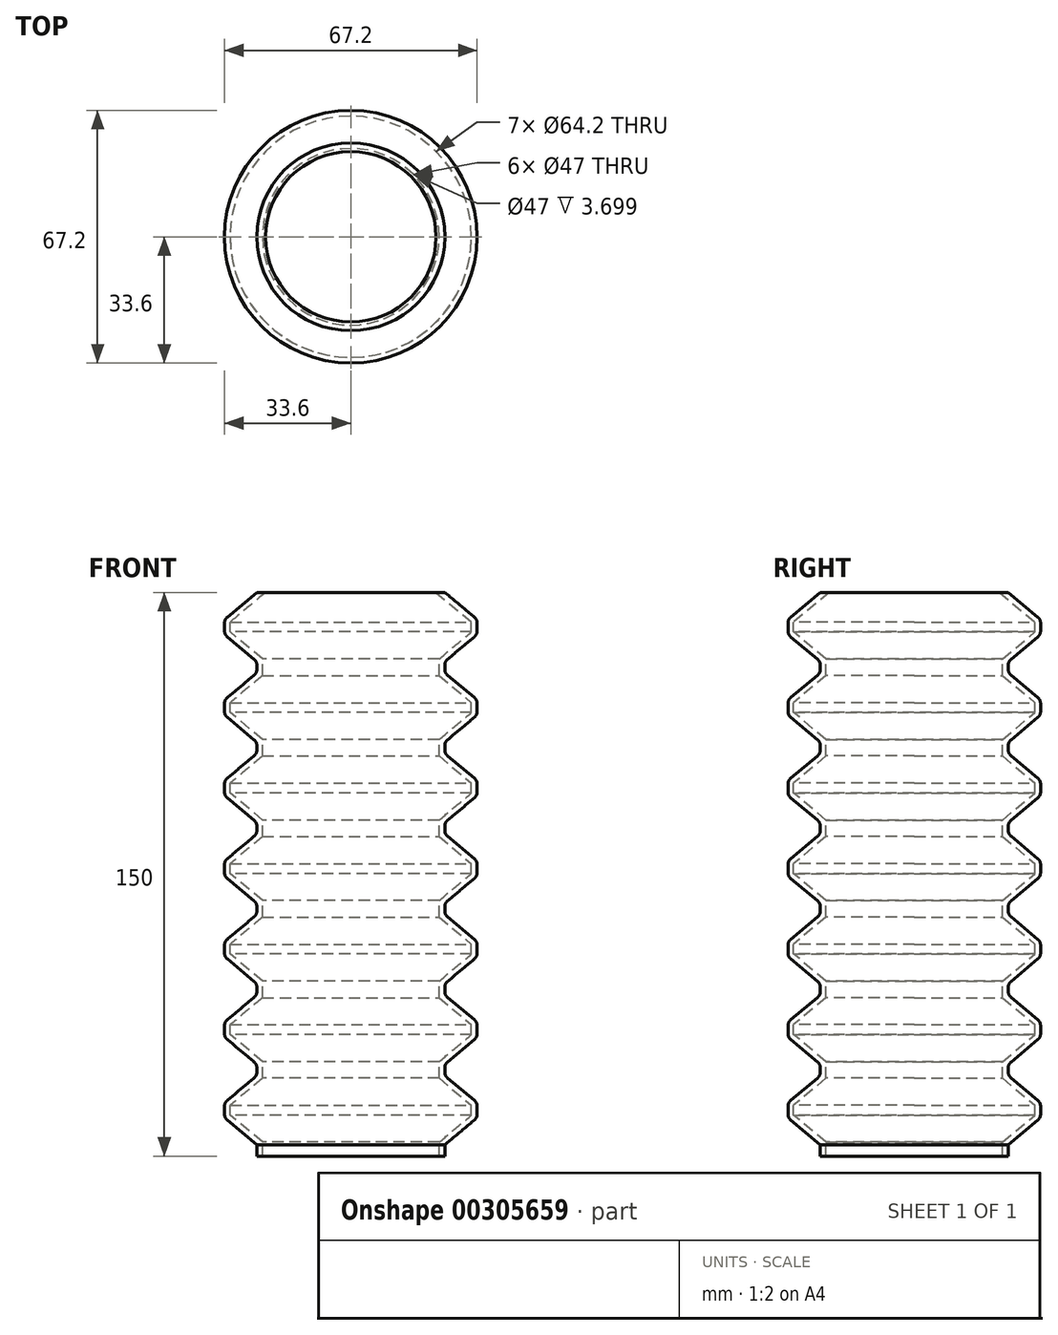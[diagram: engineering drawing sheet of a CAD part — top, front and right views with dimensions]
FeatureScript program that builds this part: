
annotation { "Feature Type Name" : "Feature", "Feature Type Description" : "" }
export const myFeature = defineFeature(function(context is Context, id is Id, definition is map)
    precondition{}
    {
        {
            var Q0;
            Q0=qCreatedBy(makeId("Front.planeOp"),FACE);
            var sketch = newSketch(context, id + "F0", { "sketchPlane" : qUnion([Q0])});
            skLineSegment(sketch, "E0", {"start": v(0, 145.92) * mm, "end": v(0, -99.97) * mm, "construction": true});
            skLineSegment(sketch, "E1", {"start": v(0, -21.95) * mm, "end": v(-25, -21.95) * mm});
            skLineSegment(sketch, "E2", {"start": v(-25, -21.95) * mm, "end": v(-25, -18.95) * mm});
            skLineSegment(sketch, "E3", {"start": v(-25, -18.95) * mm, "end": v(-33.6, -11.74) * mm});
            skLineSegment(sketch, "E4", {"start": v(-33.6, -11.74) * mm, "end": v(-33.6, -7.74) * mm});
            skLineSegment(sketch, "E5", {"start": v(-25, 2.48) * mm, "end": v(-33.6, 9.7) * mm});
            skLineSegment(sketch, "E6", {"start": v(-33.6, 9.7) * mm, "end": v(-33.6, 13.7) * mm});
            skLineSegment(sketch, "E7", {"start": v(-33.6, 13.7) * mm, "end": v(-25, 20.9) * mm});
            skLineSegment(sketch, "E8", {"start": v(-25, 20.9) * mm, "end": v(-25, 23.9) * mm});
            skLineSegment(sketch, "E9", {"start": v(-25, 23.9) * mm, "end": v(-33.6, 31.12) * mm});
            skLineSegment(sketch, "E10", {"start": v(-33.6, 31.12) * mm, "end": v(-33.6, 35.12) * mm});
            skLineSegment(sketch, "E11", {"start": v(-33.6, 35.12) * mm, "end": v(-25, 42.33) * mm});
            skLineSegment(sketch, "E12", {"start": v(-25, 42.33) * mm, "end": v(-25, 45.33) * mm});
            skLineSegment(sketch, "E13", {"start": v(-25, 45.33) * mm, "end": v(-33.6, 52.55) * mm});
            skLineSegment(sketch, "E14", {"start": v(-33.6, 52.55) * mm, "end": v(-33.6, 56.55) * mm});
            skLineSegment(sketch, "E15", {"start": v(-33.6, 56.55) * mm, "end": v(-25, 63.76) * mm});
            skLineSegment(sketch, "E16", {"start": v(-33.6, 73.98) * mm, "end": v(-33.6, 77.98) * mm});
            skLineSegment(sketch, "E17", {"start": v(-33.6, 77.98) * mm, "end": v(-25, 85.2) * mm});
            skLineSegment(sketch, "E18", {"start": v(-25, 85.2) * mm, "end": v(-25, 88.2) * mm});
            skLineSegment(sketch, "E19", {"start": v(-25, 88.2) * mm, "end": v(-33.6, 95.4) * mm});
            skLineSegment(sketch, "E20", {"start": v(-33.6, 95.4) * mm, "end": v(-33.6, 99.4) * mm});
            skLineSegment(sketch, "E21", {"start": v(-33.6, 99.4) * mm, "end": v(-25, 106.62) * mm});
            skLineSegment(sketch, "E22", {"start": v(-25, 106.62) * mm, "end": v(-25, 109.62) * mm});
            skLineSegment(sketch, "E23", {"start": v(-25, 109.62) * mm, "end": v(-33.6, 116.83) * mm});
            skLineSegment(sketch, "E24", {"start": v(-33.6, 116.83) * mm, "end": v(-33.6, 120.83) * mm});
            skLineSegment(sketch, "E25", {"start": v(-33.6, 120.83) * mm, "end": v(-25, 128.05) * mm});
            skLineSegment(sketch, "E26", {"start": v(-25, 63.76) * mm, "end": v(-25, 66.76) * mm});
            skLineSegment(sketch, "E27", {"start": v(-25, 66.76) * mm, "end": v(-33.6, 73.98) * mm});
            skLineSegment(sketch, "E28", {"start": v(-25, 2.48) * mm, "end": v(-25, -0.52) * mm});
            skLineSegment(sketch, "E29", {"start": v(-25, -0.52) * mm, "end": v(-33.6, -7.74) * mm});
            skLineSegment(sketch, "E30", {"start": v(-25, 128.05) * mm, "end": v(0, 128.05) * mm});
            skLineSegment(sketch, "E31", {"start": v(0, 128.05) * mm, "end": v(0, -21.95) * mm});
            skSolve(sketch);
        }
        {
            var Q0;
            Q0=makeQuery(id+"F0.imprint","IMPRINT",FACE,{"disambiguationData":[TD([[makeQuery(id+"F0.imprint","IMPRINT",EDGE,{"derivedFrom":sQuery(id+"F0.wireOp",EDGE,"E1")}),-1.0]])]});
            var Q1;
            Q1=sQuery(id+"F0.wireOp",EDGE,"E0");
            revolve(context, id + "F1", {"entities" : qUnion([Q0]), "axis" : qUnion([Q1]), "revolveType" : RevolveType.FULL});
        }
        {
            var Q0;
            Q0=makeQuery(id+"F1.opRevolve","SWEPT_FACE",FACE,{"disambiguationData":[OSD([sQuery(id+"F0.wireOp",EDGE,"E30")])]});
            var Q1;
            Q1=makeQuery(id+"F1.opRevolve","SWEPT_FACE",FACE,{"disambiguationData":[OSD([sQuery(id+"F0.wireOp",EDGE,"E1")])]});
            shell(context, id + "F2", {"entities" : qUnion([Q0, Q1]), "thickness" : 1.5 * mm});
        }
        {
            var Q0;
            Q0=makeQuery(id+"F1.opRevolve","SWEPT_FACE",FACE,{"disambiguationData":[OSD([sQuery(id+"F0.wireOp",EDGE,"E24")])]});
            var Q1;
            Q1=makeQuery(id+"F1.opRevolve","SWEPT_FACE",FACE,{"disambiguationData":[OSD([sQuery(id+"F0.wireOp",EDGE,"E20")])]});
            var Q2;
            Q2=makeQuery(id+"F1.opRevolve","SWEPT_FACE",FACE,{"disambiguationData":[OSD([sQuery(id+"F0.wireOp",EDGE,"E16")])]});
            var Q3;
            Q3=makeQuery(id+"F1.opRevolve","SWEPT_FACE",FACE,{"disambiguationData":[OSD([sQuery(id+"F0.wireOp",EDGE,"E14")])]});
            var Q4;
            Q4=makeQuery(id+"F1.opRevolve","SWEPT_FACE",FACE,{"disambiguationData":[OSD([sQuery(id+"F0.wireOp",EDGE,"E10")])]});
            var Q5;
            Q5=makeQuery(id+"F1.opRevolve","SWEPT_FACE",FACE,{"disambiguationData":[OSD([sQuery(id+"F0.wireOp",EDGE,"E6")])]});
            var Q6;
            Q6=makeQuery(id+"F1.opRevolve","SWEPT_FACE",FACE,{"disambiguationData":[OSD([sQuery(id+"F0.wireOp",EDGE,"E4")])]});
            fillet(context, id + "F3", {"entities" : qUnion([Q0, Q1, Q2, Q3, Q4, Q5, Q6]), "radius" : 2 * mm, "tangentPropagation" : true, "allowEdgeOverflow" : false});
        }
        {
            var Q0;
            Q0=makeQuery(id+"F1.opRevolve","SWEPT_FACE",FACE,{"disambiguationData":[OSD([sQuery(id+"F0.wireOp",EDGE,"E22")])]});
            var Q1;
            Q1=makeQuery(id+"F1.opRevolve","SWEPT_FACE",FACE,{"disambiguationData":[OSD([sQuery(id+"F0.wireOp",EDGE,"E18")])]});
            var Q2;
            Q2=makeQuery(id+"F1.opRevolve","SWEPT_FACE",FACE,{"disambiguationData":[OSD([sQuery(id+"F0.wireOp",EDGE,"E26")])]});
            var Q3;
            Q3=makeQuery(id+"F1.opRevolve","SWEPT_FACE",FACE,{"disambiguationData":[OSD([sQuery(id+"F0.wireOp",EDGE,"E12")])]});
            var Q4;
            Q4=makeQuery(id+"F1.opRevolve","SWEPT_FACE",FACE,{"disambiguationData":[OSD([sQuery(id+"F0.wireOp",EDGE,"E8")])]});
            var Q5;
            Q5=makeQuery(id+"F1.opRevolve","SWEPT_FACE",FACE,{"disambiguationData":[OSD([sQuery(id+"F0.wireOp",EDGE,"E28")])]});
            fillet(context, id + "F4", {"entities" : qUnion([Q0, Q1, Q2, Q3, Q4, Q5]), "radius" : 2 * mm, "tangentPropagation" : true, "allowEdgeOverflow" : false});
        }
    });
